# Revit family: LAMP_PUZZLE RE FRAME
name_source: partatom
category: Modelos genéricos
revit_build: Autodesk Revit 2015 (Build: 20140606_1530(x64)
units: mm (PartAtom-declared; Revit-internal decimal feet)

## types (14) — shared parameters
Accessory Type = Assembly
Comentarios de tipo = Availability of changing between standard frame Types when placed in a project.
Elevación por defecto = 1219 mm
Fabricante = LAMP
Installation instructions = http://www.lamp.es
Last update = 24/07/2018
Manufacturer URL = http://www.lamp.es
Manufacturer country = Spain
Manufacturer name = LAMP
Model explanation = Availability of changing between standard frame Types when placed in a project.
Product datasheet = http://www.lamp.es

## per-type parameters (varying)
| type | Descripción | Dimensions | Dist. A Exterior | Dist. A Interior | Dist. B Exterior | Dist. B Interior | Dist. anclaje | Finish | Material marco | Modelo | Product code | Recessed dimensions | Weight |
| TYPE 1 GREY | PUZZLE ACC. REC FRAME Nº1 GR. | 186 x 186 | 186 mm  [stored 0.610236 ft] | 142 mm  [stored 0.465879 ft] | 186 mm  [stored 0.610236 ft] | 142 mm  [stored 0.465879 ft] | 81 mm | Gloss grey | LAMP_Aluminio frame Puzzle GR | PUREFR1G | PUREFR1G | 174 x 174 | 0.24 kg |
| TYPE 1 WHITE | PUZZLE ACC. REC FRAME Nº1 WH. | 186 x 186 | 186 mm  [stored 0.610236 ft] | 142 mm  [stored 0.465879 ft] | 186 mm  [stored 0.610236 ft] | 142 mm  [stored 0.465879 ft] | 81 mm | Shiny white | LAMP_Aluminio frame Puzzle WH | PUREFR1W | PUREFR1W | 174 x 174 | 0.24 kg |
| TYPE 2 GREY | PUZZLE ACC. REC FRAME Nº2 GR. | 344 x 190 | 344 mm  [stored 1.12861 ft] | 300 mm  [stored 0.984252 ft] | 190 mm | 146 mm | 81 mm | Gloss grey | LAMP_Aluminio frame Puzzle GR | PUREFR2G | PUREFR2G | 332 x 178 | 0.45 kg |
| TYPE 2 WHITE | PUZZLE ACC. REC FRAME Nº2 WH. | 344 x 190 | 344 mm  [stored 1.12861 ft] | 300 mm  [stored 0.984252 ft] | 190 mm | 146 mm | 81 mm | Shiny white | LAMP_Aluminio frame Puzzle WH | PUREFR2W | PUREFR2W | 332 x 178 | 0.45 kg |
| TYPE 3 GREY | PUZZLE ACC. REC FRAME Nº3 GR. | 494 x 190 | 494 mm | 450 mm  [stored 1.47638 ft] | 190 mm | 146 mm | 81 mm | Gloss grey | LAMP_Aluminio frame Puzzle GR | PUREFR3G | PUREFR3G | 482 x 178 | 0.54 kg |
| TYPE 3 WHITE | PUZZLE ACC. REC FRAME Nº3 WH. | 494 x 190 | 494 mm | 450 mm  [stored 1.47638 ft] | 190 mm | 146 mm | 81 mm | Shiny white | LAMP_Aluminio frame Puzzle WH | PUREFR3W | PUREFR3W | 482 x 178 | 0.54 kg |
| TYPE 4 GREY | PUZZLE ACC. REC FRAME Nº4 GR. | 654 x 190 | 654 mm | 610 mm  [stored 2.00131 ft] | 190 mm | 146 mm | 81 mm | Gloss grey | LAMP_Aluminio frame Puzzle GR | PUREFR4G | PUREFR4G | 642 x 178 | 0.66 kg |
| TYPE 4 WHITE | PUZZLE ACC. REC FRAME Nº4 WH. | 654 x 190 | 654 mm | 610 mm  [stored 2.00131 ft] | 190 mm | 146 mm | 81 mm | Shiny white | LAMP_Aluminio frame Puzzle WH | PUREFR4W | PUREFR4W | 642 x 178 | 0.64 kg |
| TYPE 5 GREY | PUZZLE ACC. REC FRAME Nº5 GR. | 959 x 190 | 959 mm  [stored 3.14633 ft] | 915 mm  [stored 3.00197 ft] | 190 mm | 146 mm | 81 mm | Gloss grey | LAMP_Aluminio frame Puzzle GR | PUREFR5G | PUREFR5G | 974 x 178 | 0.86 kg |
| TYPE 5 WHITE | PUZZLE ACC. REC FRAME Nº5 WH. | 959 x 190 | 959 mm  [stored 3.14633 ft] | 915 mm  [stored 3.00197 ft] | 190 mm | 146 mm | 81 mm | Shiny white | LAMP_Aluminio frame Puzzle WH | PUREFR5W | PUREFR5W | 974 x 178 | 0.86 kg |
| TYPE 6 GREY | PUZZLE ACC. REC FRAME Nº6 GR. | 1264 x 190 | 1264 mm | 1220 mm  [stored 4.00262 ft] | 190 mm | 146 mm | 81 mm | Gloss grey | LAMP_Aluminio frame Puzzle GR | PUREFR6G | PUREFR6G | 1252 x 178 | 1.05 kg |
| TYPE 6 WHITE | PUZZLE ACC. REC FRAME Nº6 WH. | 1264 x 190 | 1264 mm | 1220 mm  [stored 4.00262 ft] | 190 mm | 146 mm | 81 mm | Shiny white | LAMP_Aluminio frame Puzzle WH | PUREFR6W | PUREFR6W | 1252 x 178 | 1.03 kg |
| TYPE 9 GREY | PUZZLE ACC. REC FRAME Nº9 GR. | 344 x 344 | 344 mm  [stored 1.12861 ft] | 300 mm  [stored 0.984252 ft] | 344 mm  [stored 1.12861 ft] | 300 mm  [stored 0.984252 ft] | 160 mm  [stored 0.524934 ft] | Gloss grey | LAMP_Aluminio frame Puzzle GR | PUREFR9G | PUREFR9G | 332 x 332 | 0.55 kg |
| TYPE 9 WHITE | PUZZLE ACC. REC FRAME Nº9 WH. | 344 x 344 | 344 mm  [stored 1.12861 ft] | 300 mm  [stored 0.984252 ft] | 344 mm  [stored 1.12861 ft] | 300 mm  [stored 0.984252 ft] | 160 mm  [stored 0.524934 ft] | Shiny white | LAMP_Aluminio frame Puzzle WH | PUREFR9W | PUREFR9W | 332 x 332 | 0.30 kg |

note: [stored X ft] marks values corroborated as IEEE doubles in the binary element streams (Revit-internal decimal feet)
